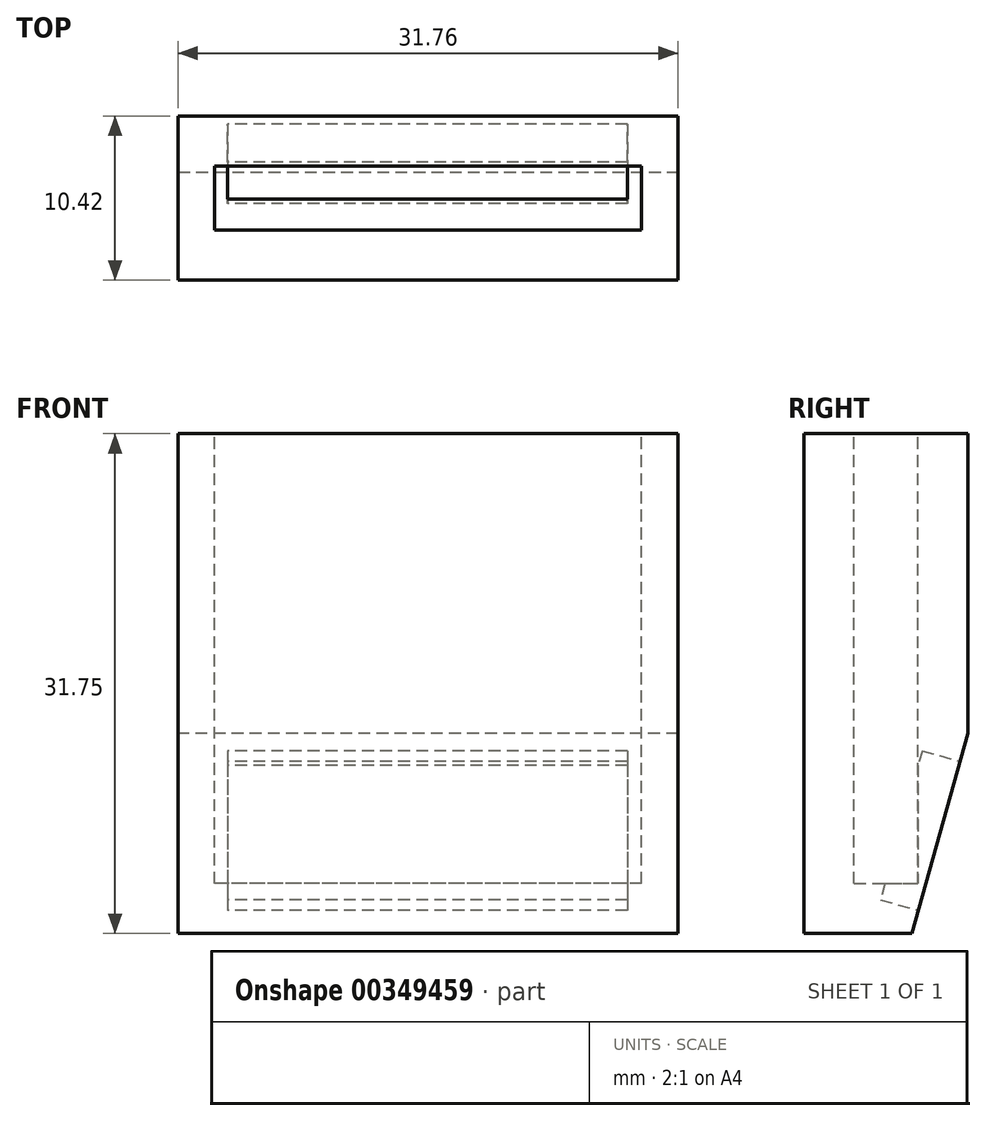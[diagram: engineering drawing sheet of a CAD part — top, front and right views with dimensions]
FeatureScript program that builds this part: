
annotation { "Feature Type Name" : "Feature", "Feature Type Description" : "" }
export const myFeature = defineFeature(function(context is Context, id is Id, definition is map)
    precondition{}
    {
        {
            var Q0;
            Q0=qCreatedBy(makeId("Top.planeOp"),FACE);
            var sketch = newSketch(context, id + "F0", { "sketchPlane" : qUnion([Q0])});
            skLineSegment(sketch, "E0.bottom", {"start": v(15.88, -5.2) * mm, "end": v(-15.88, -5.2) * mm});
            skLineSegment(sketch, "E0.top", {"start": v(15.88, 5.2) * mm, "end": v(-15.88, 5.2) * mm});
            skLineSegment(sketch, "E0.left", {"start": v(15.88, -5.2) * mm, "end": v(15.88, 5.2) * mm});
            skLineSegment(sketch, "E0.right", {"start": v(-15.88, -5.2) * mm, "end": v(-15.88, 5.2) * mm});
            skPoint(sketch, "E0.middle", {"position": v(0, 0) * mm});
            skSolve(sketch);
        }
        {
            var Q0;
            Q0=makeQuery(id+"F0.imprint","IMPRINT",FACE,{"disambiguationData":[TD([[makeQuery(id+"F0.imprint","IMPRINT",EDGE,{"derivedFrom":sQuery(id+"F0.wireOp",EDGE,"E0.bottom")}),-1.0]])]});
            extrude(context, id + "F1", {"entities" : qUnion([Q0]), "depth" : 31.75 * mm});
        }
        {
            var Q0;
            Q0=makeQuery(id+"F1.opExtrude","CAP_FACE",FACE,{"disambiguationData":[OSD([sQuery(id+"F0.wireOp",EDGE,"E0.bottom"),sQuery(id+"F0.wireOp",EDGE,"E0.top"),sQuery(id+"F0.wireOp",EDGE,"E0.left"),sQuery(id+"F0.wireOp",EDGE,"E0.right")])],"isStart":false});
            var sketch = newSketch(context, id + "F2", { "sketchPlane" : qUnion([Q0])});
            skLineSegment(sketch, "E1.bottom", {"start": v(13.56, -2.03) * mm, "end": v(-13.56, -2.03) * mm});
            skLineSegment(sketch, "E1.top", {"start": v(13.56, 2.03) * mm, "end": v(-13.56, 2.03) * mm});
            skLineSegment(sketch, "E1.left", {"start": v(13.56, -2.03) * mm, "end": v(13.56, 2.03) * mm});
            skLineSegment(sketch, "E1.right", {"start": v(-13.56, -2.03) * mm, "end": v(-13.56, 2.03) * mm});
            skPoint(sketch, "E1.middle", {"position": v(0, 0) * mm});
            skSolve(sketch);
        }
        {
            var Q0;
            Q0=makeQuery(id+"F2.imprint","IMPRINT",FACE,{"disambiguationData":[TD([[makeQuery(id+"F2.imprint","IMPRINT",EDGE,{"derivedFrom":sQuery(id+"F2.wireOp",EDGE,"E1.bottom")}),-1.0]])]});
            extrude(context, id + "F3", {"entities" : qUnion([Q0]), "operationType" : NewBodyOperationType.REMOVE, "oppositeDirection" : true, "depth" : 28.57 * mm});
        }
        {
            var Q0;
            Q0=makeQuery(id+"F1.opExtrude","CAP_EDGE",EDGE,{"disambiguationData":[OSD([sQuery(id+"F0.wireOp",EDGE,"E0.top")])],"isStart":true});
            chamfer(context, id + "F4", {"entities" : qUnion([Q0]), "chamferType" : ChamferType.TWO_OFFSETS, "width1" : 12.7 * mm, "oppositeDirection" : false, "width2" : 3.56 * mm, "tangentPropagation" : true});
        }
        {
            var Q0;
            Q0=makeQuery(id+"F4.opChamfer","BLEND_FACE",FACE,{"disambiguationData":[OSD([sQuery(id+"F0.wireOp",EDGE,"E0.top")])]});
            var sketch = newSketch(context, id + "F5", { "sketchPlane" : qUnion([Q0])});
            skLineSegment(sketch, "E2.bottom", {"start": v(-12.65, 11.8) * mm, "end": v(12.75, 11.8) * mm});
            skLineSegment(sketch, "E2.top", {"start": v(-12.65, 1.96) * mm, "end": v(12.75, 1.96) * mm});
            skLineSegment(sketch, "E2.left", {"start": v(-12.65, 11.8) * mm, "end": v(-12.65, 1.96) * mm});
            skLineSegment(sketch, "E2.right", {"start": v(12.75, 11.8) * mm, "end": v(12.75, 1.96) * mm});
            skSolve(sketch);
        }
        {
            var Q0;
            Q0 = qSketchRegion(id + "F5", true);
            extrude(context, id + "F6", {"entities" : qUnion([Q0]), "operationType" : NewBodyOperationType.REMOVE, "oppositeDirection" : true, "depth" : 2.5 * mm});
        }
    });
